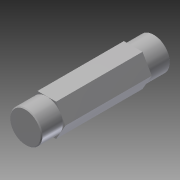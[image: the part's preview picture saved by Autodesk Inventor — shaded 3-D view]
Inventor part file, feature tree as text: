
AUTODESK INVENTOR PART (.ipt)
format: ipt  version: 2014 (Build 180170000, 170)  size: 101,888 bytes
history: native  units: in
note: dims shown in document units (in); Inventor stores cm internally (conversion verified against a paired STEP export)
features: extrude x2, sketch x2, plane x1, mirror x1, chamfer x1
ambient origin geometry x8: Origin, YZ Plane, XZ Plane, XY Plane, X Axis, Y Axis, Z Axis, Center Point
bodies: Solid1 (feature_tree)
feature tree (7):
  extrude  "Extrusion1"  Depth=1.5in TaperAngle=0.0deg
  extrude  "Extrusion2"  Depth=0.2475in TaperAngle=0.0deg
  plane  "Work Plane1"
  mirror  "Mirror1"
  chamfer  "Chamfer1"  Distance=0.01in Angle=45.0deg
  sketch  "Sketch1"  dims[d0=0.375in d1=1.5in d2=0.0in]
  sketch  "Sketch2"  dims[d3=0.374in d5=0.2475in d6=0.0in d7=0.01in d8=0.125in d9=45.0deg]
